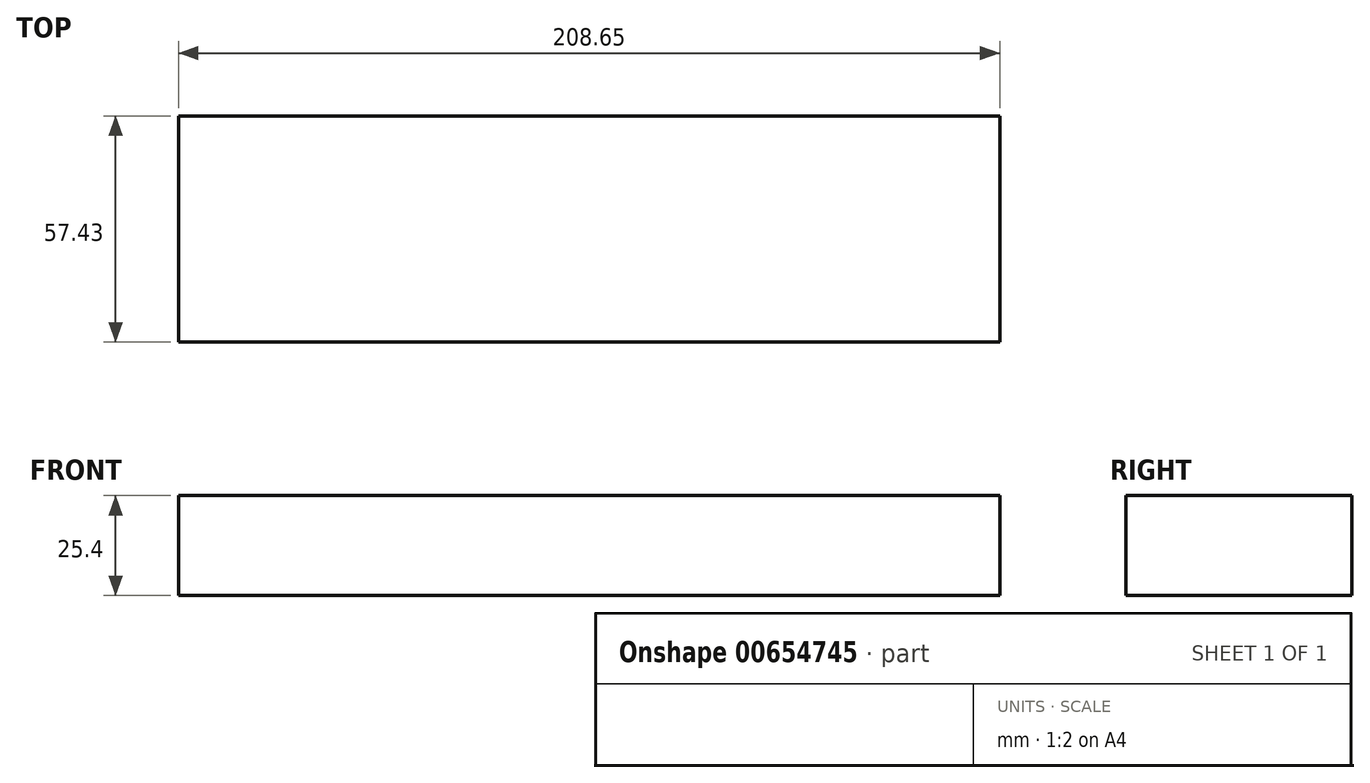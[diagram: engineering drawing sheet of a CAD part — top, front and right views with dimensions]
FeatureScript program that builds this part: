
annotation { "Feature Type Name" : "Feature", "Feature Type Description" : "" }
export const myFeature = defineFeature(function(context is Context, id is Id, definition is map)
    precondition{}
    {
        {
            var Q0;
            Q0=qCreatedBy(makeId("Top.planeOp"),FACE);
            var sketch = newSketch(context, id + "F0", { "sketchPlane" : qUnion([Q0])});
            skLineSegment(sketch, "E0.bottom", {"start": v(0, 0) * mm, "end": v(208.65, 0) * mm});
            skLineSegment(sketch, "E0.top", {"start": v(0, -57.43) * mm, "end": v(208.65, -57.43) * mm});
            skLineSegment(sketch, "E0.left", {"start": v(0, 0) * mm, "end": v(0, -57.43) * mm});
            skLineSegment(sketch, "E0.right", {"start": v(208.65, 0) * mm, "end": v(208.65, -57.43) * mm});
            skSolve(sketch);
        }
        {
            var Q0;
            Q0=makeQuery(id+"F0.imprint","IMPRINT",FACE,{"disambiguationData":[TD([[makeQuery(id+"F0.imprint","IMPRINT",EDGE,{"derivedFrom":sQuery(id+"F0.wireOp",EDGE,"E0.bottom")}),-1.0]])]});
            var sketch = newSketch(context, id + "F1", { "sketchPlane" : qUnion([Q0])});
            skSolve(sketch);
        }
        {
            var Q0;
            Q0=makeQuery(id+"F1.imprint","IMPRINT",FACE,{"disambiguationData":[TD([[makeQuery(id+"F1.imprint","IMPRINT",EDGE,{"derivedFrom":makeQuery(id+"F0.imprint","IMPRINT",EDGE,{"derivedFrom":sQuery(id+"F0.wireOp",EDGE,"E0.bottom")})}),-1.0]])]});
            extrude(context, id + "F2", {"entities" : qUnion([Q0]), "depth" : 25.4 * mm, "offsetDistance" : 25.4 * mm});
        }
    });
